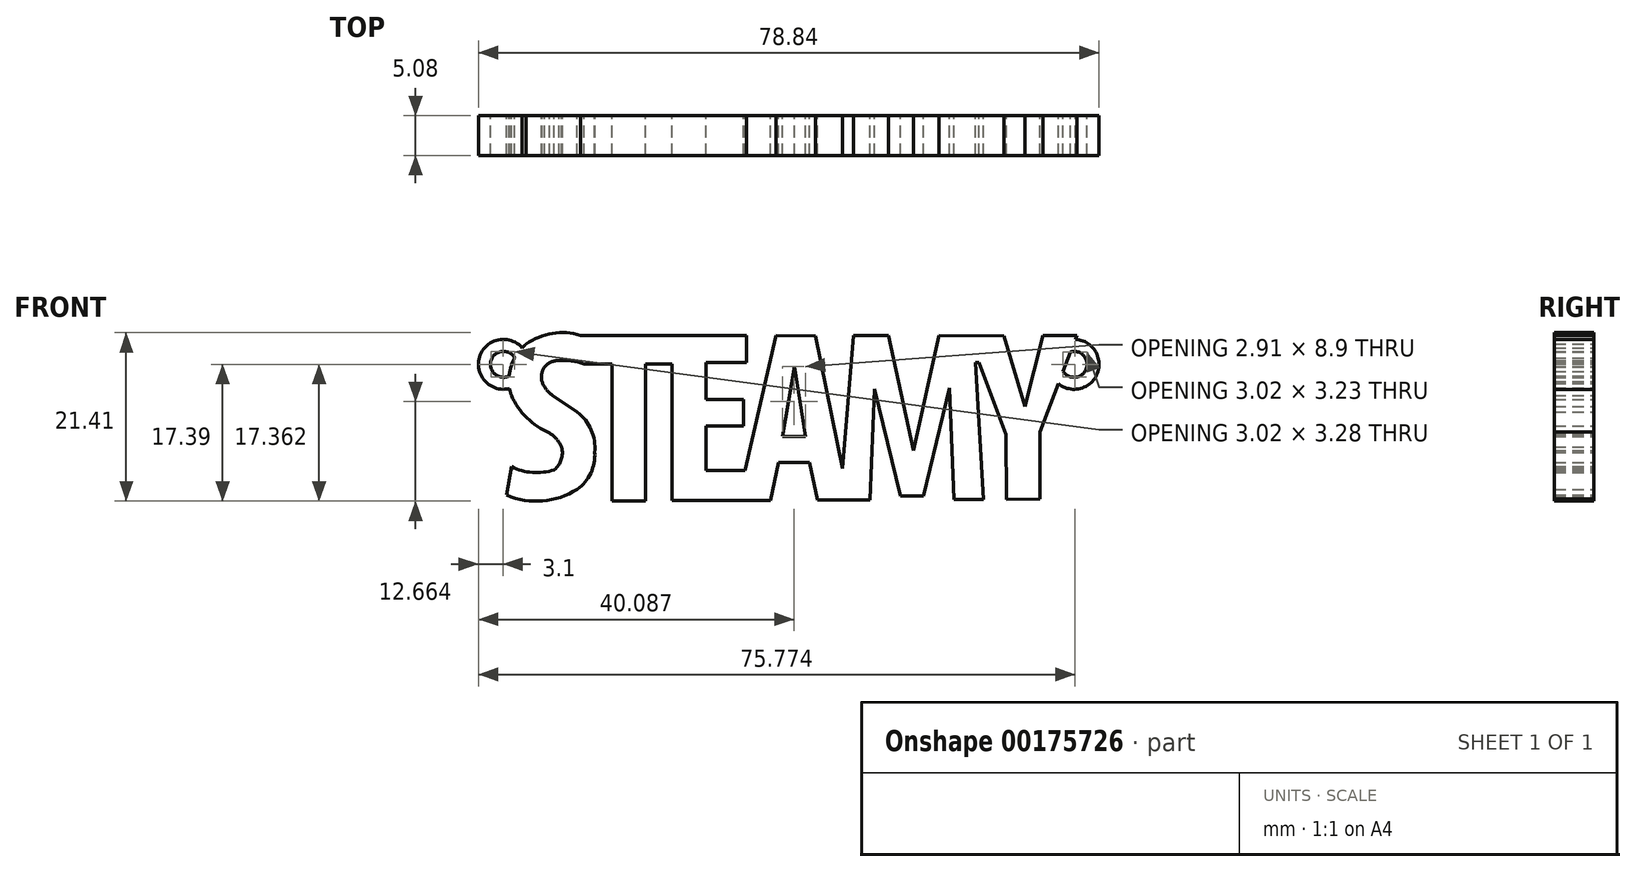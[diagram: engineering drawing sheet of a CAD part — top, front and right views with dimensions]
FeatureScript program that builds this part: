
annotation { "Feature Type Name" : "Feature", "Feature Type Description" : "" }
export const myFeature = defineFeature(function(context is Context, id is Id, definition is map)
    precondition{}
    {
        {
            var Q0;
            Q0=qCreatedBy(makeId("Front.planeOp"),FACE);
            var sketch = newSketch(context, id + "F0", { "sketchPlane" : qUnion([Q0])});
            skArc(sketch, "E0", {"start": v(-20.55, 7.62) * mm, "mid": v(-24.15, 7.86) * mm, "end": v(-27.48, 6.5) * mm});
            skArc(sketch, "E1", {"start": v(-27.48, 6.5) * mm, "mid": v(-27.74, 6.27) * mm, "end": v(-27.98, 6.04) * mm});
            skArc(sketch, "E2", {"start": v(-29.36, 0) * mm, "mid": v(-27.38, -2.86) * mm, "end": v(-24.5, -4.81) * mm});
            skArc(sketch, "E3", {"start": v(-22.97, -6.6) * mm, "mid": v(-23.6, -5.58) * mm, "end": v(-24.5, -4.81) * mm});
            skArc(sketch, "E4", {"start": v(-23.91, -9.47) * mm, "mid": v(-23.01, -8.17) * mm, "end": v(-22.97, -6.6) * mm});
            skArc(sketch, "E5", {"start": v(-29.36, -9.07) * mm, "mid": v(-26.68, -9.8) * mm, "end": v(-23.91, -9.47) * mm});
            skLineSegment(sketch, "E6", {"start": v(-29.36, -9.07) * mm, "end": v(-29.95, -12.69) * mm});
            skArc(sketch, "E7", {"start": v(-29.95, -12.69) * mm, "mid": v(-25.38, -13.42) * mm, "end": v(-21, -11.94) * mm});
            skArc(sketch, "E8", {"start": v(-21, -11.94) * mm, "mid": v(-19.26, -9.88) * mm, "end": v(-18.76, -7.24) * mm});
            skArc(sketch, "E9", {"start": v(-18.76, -7.24) * mm, "mid": v(-19.21, -4.4) * mm, "end": v(-21, -2.14) * mm});
            skLineSegment(sketch, "E10", {"start": v(-21, -2.14) * mm, "end": v(-24.12, 0) * mm});
            skArc(sketch, "E11", {"start": v(-25.47, 1.73) * mm, "mid": v(-24.93, 0.76) * mm, "end": v(-24.12, 0) * mm});
            skArc(sketch, "E12", {"start": v(-25.12, 3.61) * mm, "mid": v(-25.5, 2.71) * mm, "end": v(-25.47, 1.73) * mm});
            skArc(sketch, "E13", {"start": v(-23.32, 4.4) * mm, "mid": v(-24.32, 4.23) * mm, "end": v(-25.12, 3.61) * mm});
            skLineSegment(sketch, "E14", {"start": v(37.79, -13.2) * mm, "end": v(33.5, -13.21) * mm});
            skArc(sketch, "E15", {"start": v(-20.11, 3.97) * mm, "mid": v(-21.69, 4.38) * mm, "end": v(-23.32, 4.4) * mm});
            skLineSegment(sketch, "E16", {"start": v(-20.11, 3.97) * mm, "end": v(-16.58, 3.97) * mm});
            skLineSegment(sketch, "E17", {"start": v(-16.58, 3.97) * mm, "end": v(-16.58, -13.41) * mm});
            skLineSegment(sketch, "E18", {"start": v(-12.28, -13.4) * mm, "end": v(-12.28, 3.97) * mm});
            skLineSegment(sketch, "E19", {"start": v(-12.28, 3.97) * mm, "end": v(-8.95, 3.98) * mm});
            skLineSegment(sketch, "E20", {"start": v(-8.95, 3.98) * mm, "end": v(-8.95, -13.38) * mm});
            skLineSegment(sketch, "E21", {"start": v(-20.55, 7.62) * mm, "end": v(0.53, 7.62) * mm});
            skLineSegment(sketch, "E22", {"start": v(0.53, 7.62) * mm, "end": v(0.53, 4.15) * mm});
            skLineSegment(sketch, "E23", {"start": v(0.53, 4.15) * mm, "end": v(-4.65, 4.15) * mm});
            skLineSegment(sketch, "E24", {"start": v(-4.65, 4.15) * mm, "end": v(-4.65, -0.52) * mm});
            skLineSegment(sketch, "E25", {"start": v(-4.65, -0.52) * mm, "end": v(0.16, -0.52) * mm});
            skLineSegment(sketch, "E26", {"start": v(0.16, -0.52) * mm, "end": v(0.16, -3.92) * mm});
            skLineSegment(sketch, "E27", {"start": v(0.16, -3.92) * mm, "end": v(-4.65, -3.92) * mm});
            skLineSegment(sketch, "E28", {"start": v(-4.65, -3.92) * mm, "end": v(-4.65, -9.56) * mm});
            skLineSegment(sketch, "E29", {"start": v(-4.65, -9.56) * mm, "end": v(0.32, -9.56) * mm});
            skLineSegment(sketch, "E30", {"start": v(0.32, -9.56) * mm, "end": v(4.28, 7.62) * mm});
            skLineSegment(sketch, "E31", {"start": v(4.28, 7.62) * mm, "end": v(9.25, 7.56) * mm});
            skLineSegment(sketch, "E32", {"start": v(9.25, 7.56) * mm, "end": v(12.71, -9.32) * mm});
            skLineSegment(sketch, "E33", {"start": v(12.71, -9.32) * mm, "end": v(14.1, 7.62) * mm});
            skLineSegment(sketch, "E34", {"start": v(14.1, 7.62) * mm, "end": v(18.53, 7.58) * mm});
            skLineSegment(sketch, "E35", {"start": v(18.53, 7.58) * mm, "end": v(21.72, -7) * mm});
            skLineSegment(sketch, "E36", {"start": v(21.72, -7) * mm, "end": v(24.94, 7.62) * mm});
            skLineSegment(sketch, "E37", {"start": v(24.94, 7.62) * mm, "end": v(33.19, 7.56) * mm});
            skLineSegment(sketch, "E38", {"start": v(33.19, 7.56) * mm, "end": v(35.87, -1.4) * mm});
            skLineSegment(sketch, "E39", {"start": v(35.87, -1.4) * mm, "end": v(38.16, 7.62) * mm});
            skLineSegment(sketch, "E40", {"start": v(38.16, 7.62) * mm, "end": v(42.46, 7.6) * mm});
            skLineSegment(sketch, "E41", {"start": v(42.46, 7.6) * mm, "end": v(42.28, 7.1) * mm});
            skLineSegment(sketch, "E42", {"start": v(37.77, -4.67) * mm, "end": v(37.79, -13.2) * mm});
            skLineSegment(sketch, "E43", {"start": v(5.1, -5.24) * mm, "end": v(8, -5.23) * mm});
            skLineSegment(sketch, "E44", {"start": v(8, -5.23) * mm, "end": v(6.63, 3.66) * mm});
            skLineSegment(sketch, "E45", {"start": v(6.63, 3.66) * mm, "end": v(5.1, -5.24) * mm});
            skLineSegment(sketch, "E46", {"start": v(3.56, -13.33) * mm, "end": v(4.6, -8.5) * mm});
            skLineSegment(sketch, "E47", {"start": v(4.6, -8.5) * mm, "end": v(8.52, -8.5) * mm});
            skLineSegment(sketch, "E48", {"start": v(8.52, -8.5) * mm, "end": v(9.5, -13.3) * mm});
            skLineSegment(sketch, "E49", {"start": v(16.2, -13.28) * mm, "end": v(16.76, 0.8) * mm});
            skLineSegment(sketch, "E50", {"start": v(16.76, 0.8) * mm, "end": v(20.1, -12.77) * mm});
            skLineSegment(sketch, "E51", {"start": v(20.1, -12.77) * mm, "end": v(22.98, -12.76) * mm});
            skLineSegment(sketch, "E52", {"start": v(22.98, -12.76) * mm, "end": v(26.28, 0.94) * mm});
            skLineSegment(sketch, "E53", {"start": v(26.28, 0.94) * mm, "end": v(26.87, -13.24) * mm});
            skLineSegment(sketch, "E54", {"start": v(30.6, -13.22) * mm, "end": v(29.62, 4.14) * mm});
            skLineSegment(sketch, "E55", {"start": v(30.07, 4.14) * mm, "end": v(33.47, -4.99) * mm});
            skLineSegment(sketch, "E56", {"start": v(33.47, -4.99) * mm, "end": v(33.5, -13.21) * mm});
            skArc(sketch, "E57", {"start": v(-27.98, 6.04) * mm, "mid": v(-33.4, 4.87) * mm, "end": v(-29.58, 0.86) * mm});
            skArc(sketch, "E58", {"start": v(-28.93, 4.76) * mm, "mid": v(-31.94, 4.43) * mm, "end": v(-29.64, 2.45) * mm});
            skArc(sketch, "E59", {"start": v(40.73, 3.06) * mm, "mid": v(43.66, 3.35) * mm, "end": v(41.67, 5.53) * mm});
            skArc(sketch, "E60", {"start": v(40.12, 1.47) * mm, "mid": v(45.09, 2.8) * mm, "end": v(42.28, 7.1) * mm});
            skLineSegment(sketch, "E61", {"start": v(29.62, 4.14) * mm, "end": v(30.07, 4.14) * mm});
            skLineSegment(sketch, "E62.trimOffspring", {"start": v(-12.28, -13.4) * mm, "end": v(-16.58, -13.41) * mm});
            skLineSegment(sketch, "E63.trimOffspring", {"start": v(3.56, -13.33) * mm, "end": v(-8.95, -13.38) * mm});
            skLineSegment(sketch, "E64.trimOffspring", {"start": v(16.2, -13.28) * mm, "end": v(9.5, -13.3) * mm});
            skLineSegment(sketch, "E65.trimOffspring", {"start": v(30.6, -13.22) * mm, "end": v(26.87, -13.24) * mm});
            skLineSegment(sketch, "E66.trimOffspring", {"start": v(41.67, 5.53) * mm, "end": v(40.73, 3.06) * mm});
            skLineSegment(sketch, "E67.trimOffspring", {"start": v(40.12, 1.47) * mm, "end": v(37.77, -4.67) * mm});
            skArc(sketch, "E68.trimOffspring", {"start": v(-28.93, 4.76) * mm, "mid": v(-29.4, 3.64) * mm, "end": v(-29.64, 2.45) * mm});
            skArc(sketch, "E69.trimOffspring", {"start": v(-29.58, 0.86) * mm, "mid": v(-29.49, 0.43) * mm, "end": v(-29.36, 0) * mm});
            skSolve(sketch);
        }
        {
            var Q0;
            Q0=makeQuery(id+"F0.imprint","IMPRINT",FACE,{"disambiguationData":[TD([[makeQuery(id+"F0.imprint","IMPRINT",EDGE,{"derivedFrom":sQuery(id+"F0.wireOp",EDGE,"E0")}),1.0]])]});
            var Q1;
            {var subQ0=sQuery(id+"F0.wireOp",EDGE,"E57");Q1=makeQuery(id+"F0.imprint","IMPRINT",FACE,{"disambiguationData":[TD([[makeQuery(id+"F0.imprint","IMPRINT",EDGE,{"derivedFrom":subQ0}),1.0]])]});}
            var Q2;
            {var subQ0=sQuery(id+"F0.wireOp",EDGE,"BpDhYeeL-dhBW-vac3-0elO-WGnZeApBQgNL");Q2=makeQuery(id+"F0.imprint","IMPRINT",FACE,{"disambiguationData":[TD([[makeQuery(id+"F0.imprint","IMPRINT",EDGE,{"derivedFrom":subQ0}),-1.0]])]});}
            var Q3;
            {var subQ0=sQuery(id+"F0.wireOp",EDGE,"E59");Q3=makeQuery(id+"F0.imprint","IMPRINT",FACE,{"disambiguationData":[TD([[makeQuery(id+"F0.imprint","IMPRINT",EDGE,{"derivedFrom":subQ0}),-1.0]])]});}
            extrude(context, id + "F1", {"entities" : qUnion([Q0, Q1, Q2, Q3]), "depth" : 5.08 * mm});
        }
    });
